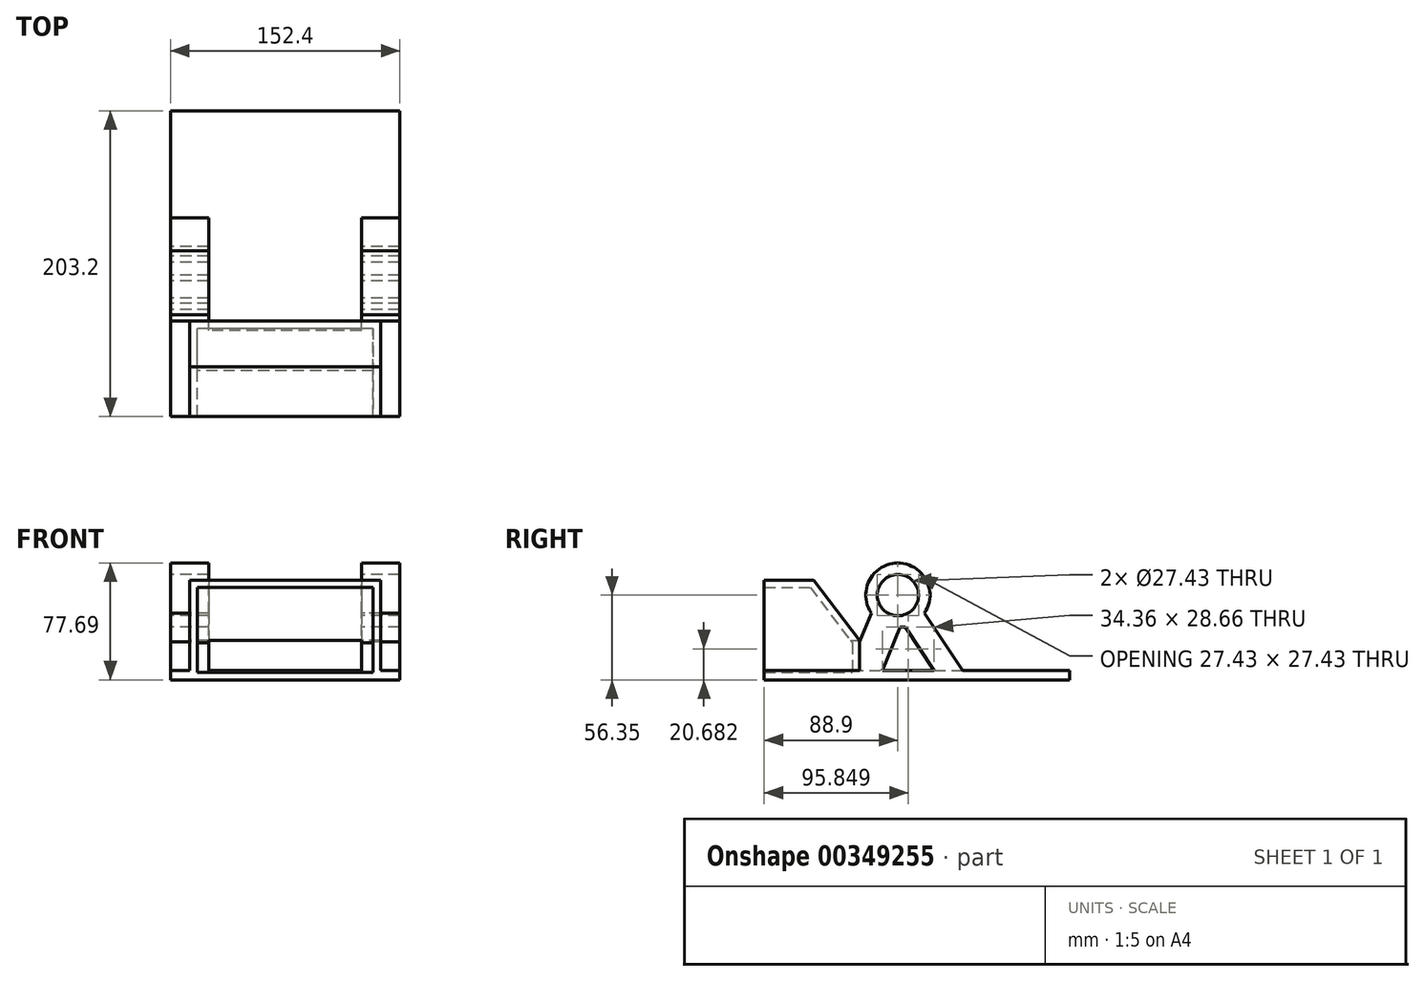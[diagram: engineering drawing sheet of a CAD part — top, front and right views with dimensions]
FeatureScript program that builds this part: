
annotation { "Feature Type Name" : "Feature", "Feature Type Description" : "" }
export const myFeature = defineFeature(function(context is Context, id is Id, definition is map)
    precondition{}
    {
        {
            var Q0;
            Q0=qCreatedBy(makeId("Top.planeOp"),FACE);
            var sketch = newSketch(context, id + "F0", { "sketchPlane" : qUnion([Q0])});
            skLineSegment(sketch, "E0.bottom", {"start": v(-76.2, 101.6) * mm, "end": v(76.2, 101.6) * mm});
            skLineSegment(sketch, "E0.top", {"start": v(-76.2, -101.6) * mm, "end": v(76.2, -101.6) * mm});
            skLineSegment(sketch, "E0.left", {"start": v(-76.2, 101.6) * mm, "end": v(-76.2, -101.6) * mm});
            skLineSegment(sketch, "E0.right", {"start": v(76.2, 101.6) * mm, "end": v(76.2, -101.6) * mm});
            skPoint(sketch, "E0.middle", {"position": v(0, 0) * mm});
            skSolve(sketch);
        }
        {
            var Q0;
            Q0 = qSketchRegion(id + "F0", true);
            extrude(context, id + "F1", {"entities" : qUnion([Q0]), "oppositeDirection" : true, "depth" : 6.35 * mm});
        }
        {
            var Q0;
            Q0=qCreatedBy(makeId("Right.planeOp"),FACE);
            var sketch = newSketch(context, id + "F2", { "sketchPlane" : qUnion([Q0])});
            skLineSegment(sketch, "E1", {"start": v(-101.6, 0) * mm, "end": v(-101.6, 60) * mm});
            skLineSegment(sketch, "E2", {"start": v(-101.6, 60) * mm, "end": v(-68.58, 60) * mm});
            skLineSegment(sketch, "E3", {"start": v(-68.58, 60) * mm, "end": v(-38.1, 20) * mm});
            skLineSegment(sketch, "E4", {"start": v(-38.1, 20) * mm, "end": v(-38.1, 0) * mm});
            skLineSegment(sketch, "E5", {"start": v(-38.1, 0) * mm, "end": v(-101.6, 0) * mm});
            skSolve(sketch);
        }
        {
            var Q0;
            Q0=makeQuery(id+"F2.imprint","IMPRINT",FACE,{"disambiguationData":[TD([[makeQuery(id+"F2.imprint","IMPRINT",EDGE,{"derivedFrom":sQuery(id+"F2.wireOp",EDGE,"E1")}),-1.0]])]});
            extrude(context, id + "F3", {"entities" : qUnion([Q0]), "operationType" : NewBodyOperationType.ADD, "endBound" : BoundingType.SYMMETRIC, "depth" : 127 * mm});
        }
        {
            var Q0;
            Q0=makeQuery(id+"F3.boolean.opBoolean","MERGE",FACE,{"derivedFrom":[makeQuery(id+"F1.opExtrude","SWEPT_FACE",FACE,{"disambiguationData":[OSD([sQuery(id+"F0.wireOp",EDGE,"E0.top")])]}),makeQuery(id+"F3.opExtrude","SWEPT_FACE",FACE,{"disambiguationData":[OSD([sQuery(id+"F2.wireOp",EDGE,"E1")])]})]});
            shell(context, id + "F4", {"entities" : qUnion([Q0]), "thickness" : 5 * mm});
        }
        {
            var Q0;
            Q0=makeQuery(id+"F3.opExtrude","SWEPT_FACE",FACE,{"disambiguationData":[OSD([sQuery(id+"F2.wireOp",EDGE,"E4")])]});
            var sketch = newSketch(context, id + "F5", { "sketchPlane" : qUnion([Q0])});
            skLineSegment(sketch, "E6.bottom", {"start": v(-50.8, 20) * mm, "end": v(50.8, 20) * mm});
            skLineSegment(sketch, "E6.top", {"start": v(-50.8, 0) * mm, "end": v(50.8, 0) * mm});
            skLineSegment(sketch, "E6.left", {"start": v(-50.8, 20) * mm, "end": v(-50.8, 0) * mm});
            skLineSegment(sketch, "E6.right", {"start": v(50.8, 20) * mm, "end": v(50.8, 0) * mm});
            skSolve(sketch);
        }
        {
            var Q0;
            Q0=qCreatedBy(makeId("Right.planeOp"),FACE);
            var sketch = newSketch(context, id + "F6", { "sketchPlane" : qUnion([Q0])});
            skCircle(sketch, "E7", {"center": v(-12.7, 50) * mm, "radius": 13.72 * mm});
            skArc(sketch, "E8", {"start": v(5, 38.1) * mm, "mid": v(-12.7, 71.34) * mm, "end": v(-30.4, 38.1) * mm});
            skLineSegment(sketch, "E9", {"start": v(-38.1, 0) * mm, "end": v(30.48, 0) * mm});
            skLineSegment(sketch, "E10", {"start": v(30.48, 0) * mm, "end": v(5, 38.1) * mm});
            skLineSegment(sketch, "E11", {"start": v(-22.93, 0) * mm, "end": v(-11.36, 28.66) * mm});
            skLineSegment(sketch, "E12", {"start": v(-11.36, 28.66) * mm, "end": v(-7.73, 28.66) * mm});
            skLineSegment(sketch, "E13", {"start": v(-7.73, 28.66) * mm, "end": v(11.43, 0) * mm});
            skLineSegment(sketch, "E14", {"start": v(11.43, 0) * mm, "end": v(-22.93, 0) * mm});
            skLineSegment(sketch, "E15", {"start": v(-30.4, 38.1) * mm, "end": v(-38.1, 19.05) * mm});
            skLineSegment(sketch, "E16", {"start": v(-38.1, 19.05) * mm, "end": v(-38.1, 0) * mm});
            skSolve(sketch);
        }
        {
            var Q0;
            Q0=makeQuery(id+"F6.imprint","IMPRINT",FACE,{"disambiguationData":[TD([[makeQuery(id+"F6.imprint","IMPRINT",EDGE,{"derivedFrom":sQuery(id+"F6.wireOp",EDGE,"E7")}),-1.0]])]});
            extrude(context, id + "F7", {"entities" : qUnion([Q0]), "operationType" : NewBodyOperationType.ADD, "endBound" : BoundingType.SYMMETRIC, "depth" : 152.4 * mm});
        }
        {
            var Q0;
            Q0=makeQuery(id+"F5.imprint","IMPRINT",FACE,{"disambiguationData":[TD([[makeQuery(id+"F5.imprint","IMPRINT",EDGE,{"derivedFrom":sQuery(id+"F5.wireOp",EDGE,"E6.bottom")}),-1.0]])]});
            extrude(context, id + "F8", {"entities" : qUnion([Q0]), "operationType" : NewBodyOperationType.REMOVE, "endBound" : BoundingType.THROUGH_ALL, "oppositeDirection" : true, "depth" : 25.4 * mm, "hasSecondDirection" : true, "secondDirectionBound" : SecondDirectionBoundingType.THROUGH_ALL, "secondDirectionOppositeDirection" : false, "secondDirectionDepth" : 25.4 * mm});
        }
        {
            var Q0;
            {var subQ4=sQuery(id+"F6.wireOp",EDGE,"E11");var subQ11=sQuery(id+"F0.wireOp",EDGE,"E0.right");var subQ13=sQuery(id+"F0.wireOp",EDGE,"E0.left");var subQ15=sQuery(id+"F0.wireOp",EDGE,"E0.bottom");var subQ16=makeQuery(id+"F1.opExtrude","CAP_FACE",FACE,{"disambiguationData":[OSD([subQ15,sQuery(id+"F0.wireOp",EDGE,"E0.top"),subQ13,subQ11])],"isStart":true});Q0=makeQuery(id+"F8.boolean.opBoolean","MERGE",FACE,{"derivedFrom":[makeQuery(id+"F7.boolean.opBoolean","SPLIT",FACE,{"disambiguationData":[TD([makeQuery(id+"F1.opExtrude","SWEPT_FACE",FACE,{"disambiguationData":[OSD([subQ15])]})])],"derivedFrom":subQ16}),makeQuery(id+"F7.boolean.opBoolean","SPLIT",FACE,{"disambiguationData":[TD([makeQuery(id+"F7.opExtrude","SWEPT_FACE",FACE,{"disambiguationData":[OSD([subQ4])]})])],"derivedFrom":subQ16}),makeQuery(id+"F8.opExtrude","SWEPT_FACE",FACE,{"disambiguationData":[OSD([sQuery(id+"F5.wireOp",EDGE,"E6.top")])]})]});}
            var sketch = newSketch(context, id + "F9", { "sketchPlane" : qUnion([Q0])});
            skLineSegment(sketch, "E17.bottom", {"start": v(50.8, 30.48) * mm, "end": v(-50.8, 30.48) * mm});
            skLineSegment(sketch, "E17.top", {"start": v(50.8, -38.1) * mm, "end": v(-50.8, -38.1) * mm});
            skLineSegment(sketch, "E17.left", {"start": v(50.8, 30.48) * mm, "end": v(50.8, -38.1) * mm});
            skLineSegment(sketch, "E17.right", {"start": v(-50.8, 30.48) * mm, "end": v(-50.8, -38.1) * mm});
            skSolve(sketch);
        }
        {
            var Q0;
            {var subQ30=sQuery(id+"F9.wireOp",EDGE,"E17.bottom");Q0=makeQuery(id+"F9.imprint","IMPRINT",FACE,{"disambiguationData":[TD([[makeQuery(id+"F9.imprint","IMPRINT",EDGE,{"derivedFrom":subQ30}),1.0]])]});}
            extrude(context, id + "F10", {"entities" : qUnion([Q0]), "operationType" : NewBodyOperationType.REMOVE, "endBound" : BoundingType.THROUGH_ALL, "depth" : 25.4 * mm});
        }
    });
